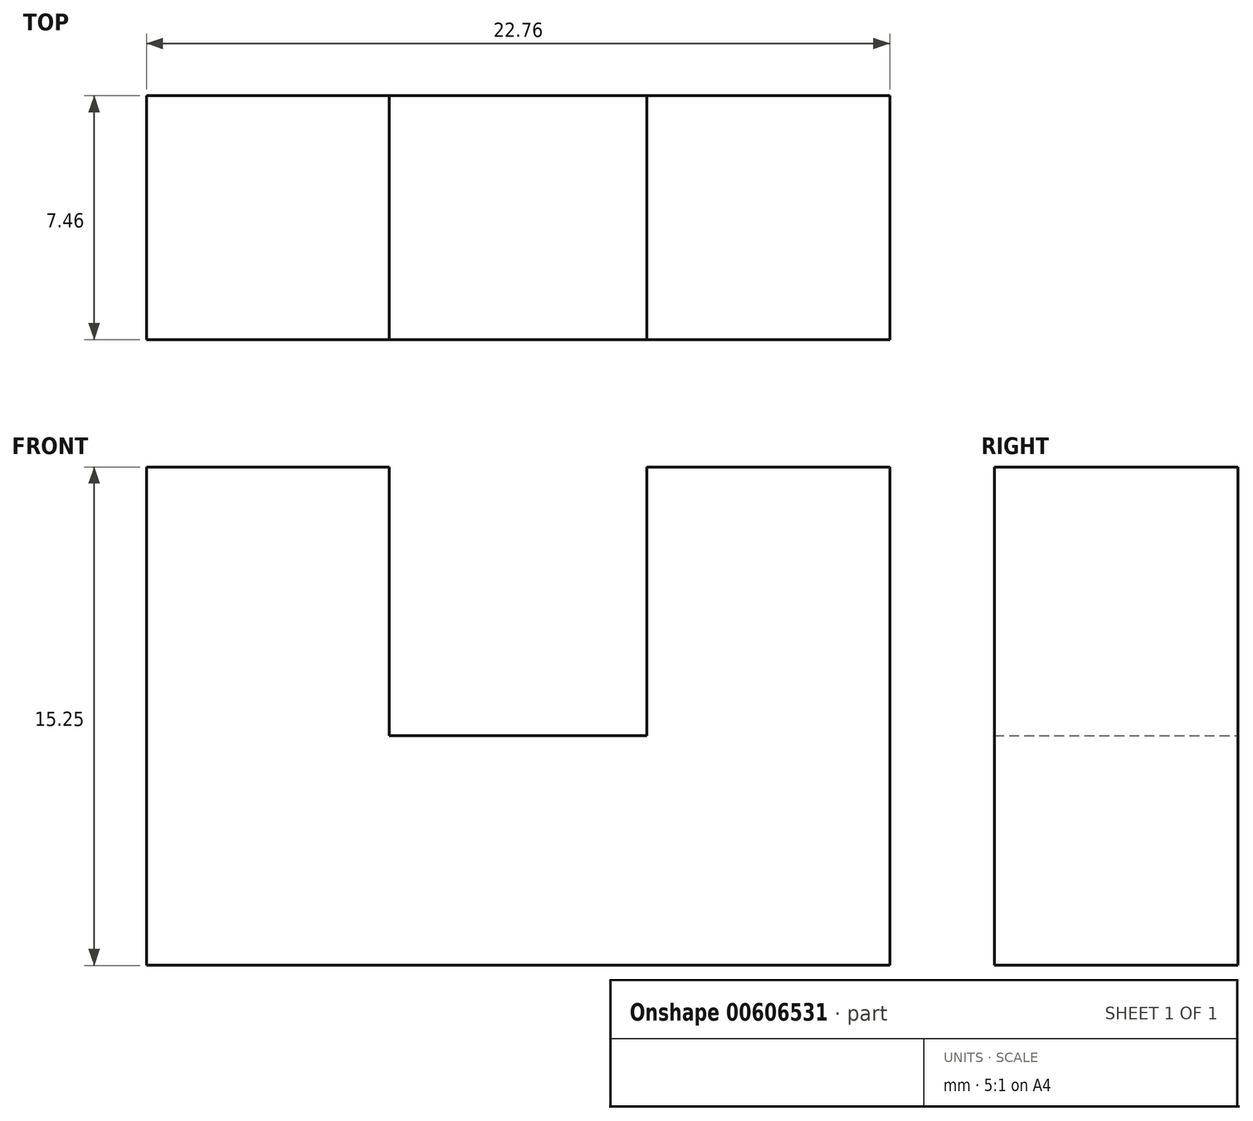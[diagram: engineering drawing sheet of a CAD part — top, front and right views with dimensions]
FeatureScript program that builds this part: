
annotation { "Feature Type Name" : "Feature", "Feature Type Description" : "" }
export const myFeature = defineFeature(function(context is Context, id is Id, definition is map)
    precondition{}
    {
        {
            var Q0;
            Q0=qCreatedBy(makeId("Front.planeOp"),FACE);
            var sketch = newSketch(context, id + "F0", { "sketchPlane" : qUnion([Q0])});
            skLineSegment(sketch, "E0", {"start": v(-22.76, 8.22) * mm, "end": v(-22.76, -7.03) * mm});
            skLineSegment(sketch, "E1", {"start": v(-22.76, -7.03) * mm, "end": v(0, -7.03) * mm});
            skLineSegment(sketch, "E2", {"start": v(0, -7.03) * mm, "end": v(0, 8.22) * mm});
            skLineSegment(sketch, "E3", {"start": v(0, 8.22) * mm, "end": v(-7.44, 8.22) * mm});
            skLineSegment(sketch, "E4", {"start": v(-7.44, 8.22) * mm, "end": v(-7.44, 0) * mm});
            skLineSegment(sketch, "E5", {"start": v(-15.32, 0) * mm, "end": v(-15.32, 8.22) * mm});
            skLineSegment(sketch, "E6", {"start": v(-15.32, 8.22) * mm, "end": v(-22.76, 8.22) * mm});
            skLineSegment(sketch, "E7", {"start": v(-15.32, 0) * mm, "end": v(-7.44, 0) * mm});
            skSolve(sketch);
        }
        {
            var Q0;
            Q0=makeQuery(id+"F0.imprint","IMPRINT",FACE,{"disambiguationData":[TD([[makeQuery(id+"F0.imprint","IMPRINT",EDGE,{"derivedFrom":sQuery(id+"F0.wireOp",EDGE,"E0")}),1.0]])]});
            extrude(context, id + "F1", {"entities" : qUnion([Q0]), "depth" : 7.46 * mm, "offsetDistance" : 25.4 * mm});
        }
    });
